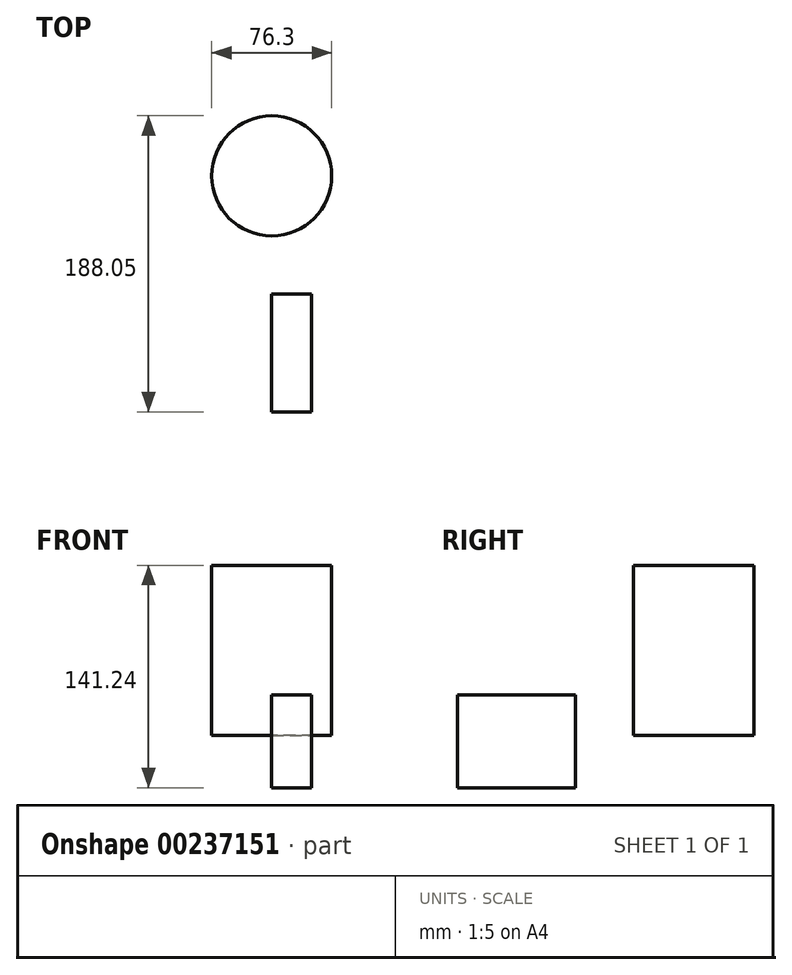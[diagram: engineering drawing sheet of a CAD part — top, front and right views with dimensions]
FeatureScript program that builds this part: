
annotation { "Feature Type Name" : "Feature", "Feature Type Description" : "" }
export const myFeature = defineFeature(function(context is Context, id is Id, definition is map)
    precondition{}
    {
        {
            var Q0;
            Q0=qCreatedBy(makeId("Top.planeOp"),FACE);
            var sketch = newSketch(context, id + "F0", { "sketchPlane" : qUnion([Q0])});
            skCircle(sketch, "E0", {"center": v(0, 0) * mm, "radius": 38.15 * mm});
            skSolve(sketch);
        }
        {
            var Q0;
            Q0=makeQuery(id+"F0.imprint","IMPRINT",FACE,{"disambiguationData":[TD([[makeQuery(id+"F0.imprint","IMPRINT",EDGE,{"derivedFrom":sQuery(id+"F0.wireOp",EDGE,"E0")}),1.0]])]});
            extrude(context, id + "F1", {"entities" : qUnion([Q0]), "depth" : 107.95 * mm});
        }
        {
            var Q0;
            Q0=qCreatedBy(makeId("Right.planeOp"),FACE);
            var sketch = newSketch(context, id + "F2", { "sketchPlane" : qUnion([Q0])});
            skLineSegment(sketch, "E1.bottom", {"start": v(-149.9, -33.3) * mm, "end": v(-75.2, -33.3) * mm});
            skLineSegment(sketch, "E1.top", {"start": v(-149.9, 25.76) * mm, "end": v(-75.2, 25.76) * mm});
            skLineSegment(sketch, "E1.left", {"start": v(-149.9, -33.3) * mm, "end": v(-149.9, 25.76) * mm});
            skLineSegment(sketch, "E1.right", {"start": v(-75.2, -33.3) * mm, "end": v(-75.2, 25.76) * mm});
            skSolve(sketch);
        }
        {
            var Q0;
            Q0=makeQuery(id+"F2.imprint","IMPRINT",FACE,{"disambiguationData":[TD([[makeQuery(id+"F2.imprint","IMPRINT",EDGE,{"derivedFrom":sQuery(id+"F2.wireOp",EDGE,"E1.bottom")}),1.0]])]});
            extrude(context, id + "F3", {"entities" : qUnion([Q0]), "depth" : 25.4 * mm});
        }
    });
